# Revit family: Royal-allas
name_source: partatom
category: Plumbing Fixtures
revit_build: Autodesk Revit 2015 (Build: 20160512_0715(x64)
units: mm (PartAtom-declared; Revit-internal decimal feet)

## types (9) — shared parameters
Assembly Code = 1336
Assembly Height = 800 mm  [stored 2.62467 ft]
Depth = 600 mm  [stored 1.9685 ft]
Frame Colour = RAL 9016 - White
Height = 180 mm  [stored 0.590551 ft]
Keynote = 523
Manufacturer = Väinö Korpinen Oy
Model = Royal
Thickness = 30 mm  [stored 0.0984252 ft]
Width = 600 mm  [stored 1.9685 ft]

## per-type parameters (varying)
| type | Colour | Electrical | Manual |
| -sähkösäätö punainen | RAL 3003 - Red | Yes | No |
| -sähkösäätö harmaa | RAL 7037 - Gray | Yes | No |
| -sähkösäätö valkoinen | RAL 9016 - White | Yes | No |
| -manuaali harmaa | RAL 7037 - Gray | No | Yes |
| -manuaali punainen | RAL 3003 - Red | No | Yes |
| -manuaali valkoinen | RAL 9016 - White | No | Yes |
| -vesilukollinen valkoinen | RAL 9016 - White | No | No |
| -vesilukollinen punainen | RAL 3003 - Red | No | No |
| -vesilukollinen harmaa | RAL 7037 - Gray | No | No |

note: [stored X ft] marks values corroborated as IEEE doubles in the binary element streams (Revit-internal decimal feet)

## geometry (parser evidence)
native form markers: Blend x4, Sweep x15
no freeform markers — native parametric forms only
